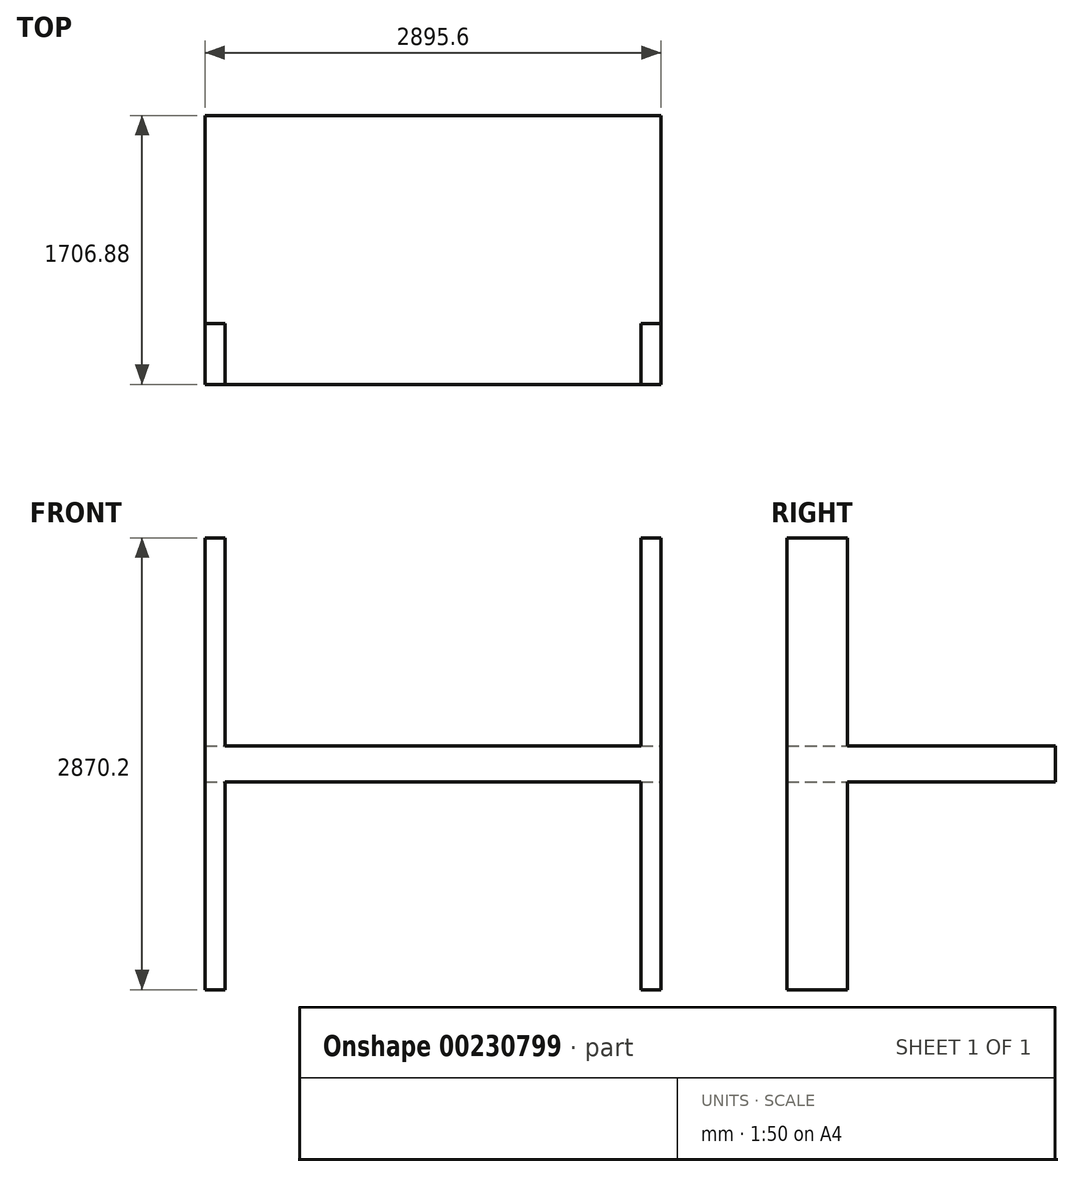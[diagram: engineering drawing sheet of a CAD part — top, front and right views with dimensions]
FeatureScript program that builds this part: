
annotation { "Feature Type Name" : "Feature", "Feature Type Description" : "" }
export const myFeature = defineFeature(function(context is Context, id is Id, definition is map)
    precondition{}
    {
        {
            var Q0;
            Q0=qCreatedBy(makeId("Front.planeOp"),FACE);
            var sketch = newSketch(context, id + "F0", { "sketchPlane" : qUnion([Q0])});
            skSolve(sketch);
        }
        {
            var Q0;
            Q0=qCreatedBy(makeId("Front.planeOp"),FACE);
            var sketch = newSketch(context, id + "F1", { "sketchPlane" : qUnion([Q0])});
            skLineSegment(sketch, "E0.bottom", {"start": v(-670.18, 381.56) * mm, "end": v(2225.42, 381.56) * mm});
            skLineSegment(sketch, "E0.top", {"start": v(-670.18, 152.96) * mm, "end": v(2225.42, 152.96) * mm});
            skLineSegment(sketch, "E0.left", {"start": v(-670.18, 381.56) * mm, "end": v(-670.18, 152.96) * mm});
            skLineSegment(sketch, "E0.right", {"start": v(2225.42, 381.56) * mm, "end": v(2225.42, 152.96) * mm});
            skLineSegment(sketch, "E1.bottom", {"start": v(-670.18, 381.56) * mm, "end": v(-543.18, 381.56) * mm});
            skLineSegment(sketch, "E1.top", {"start": v(-670.18, 1702.36) * mm, "end": v(-543.18, 1702.36) * mm});
            skLineSegment(sketch, "E1.left", {"start": v(-670.18, 381.56) * mm, "end": v(-670.18, 1702.36) * mm});
            skLineSegment(sketch, "E1.right", {"start": v(-543.18, 381.56) * mm, "end": v(-543.18, 1702.36) * mm});
            skLineSegment(sketch, "E2.bottom", {"start": v(2225.42, 381.56) * mm, "end": v(2098.42, 381.56) * mm});
            skLineSegment(sketch, "E2.top", {"start": v(2225.42, 1702.36) * mm, "end": v(2098.42, 1702.36) * mm});
            skLineSegment(sketch, "E2.left", {"start": v(2225.42, 381.56) * mm, "end": v(2225.42, 1702.36) * mm});
            skLineSegment(sketch, "E2.right", {"start": v(2098.42, 381.56) * mm, "end": v(2098.42, 1702.36) * mm});
            skLineSegment(sketch, "E3.bottom", {"start": v(-670.18, 152.96) * mm, "end": v(-543.18, 152.96) * mm});
            skLineSegment(sketch, "E3.top", {"start": v(-670.18, -1167.84) * mm, "end": v(-543.18, -1167.84) * mm});
            skLineSegment(sketch, "E3.left", {"start": v(-670.18, 152.96) * mm, "end": v(-670.18, -1167.84) * mm});
            skLineSegment(sketch, "E3.right", {"start": v(-543.18, 152.96) * mm, "end": v(-543.18, -1167.84) * mm});
            skLineSegment(sketch, "E4.bottom", {"start": v(2225.42, 152.96) * mm, "end": v(2098.42, 152.96) * mm});
            skLineSegment(sketch, "E4.top", {"start": v(2225.42, -1167.84) * mm, "end": v(2098.42, -1167.84) * mm});
            skLineSegment(sketch, "E4.left", {"start": v(2225.42, 152.96) * mm, "end": v(2225.42, -1167.84) * mm});
            skLineSegment(sketch, "E4.right", {"start": v(2098.42, 152.96) * mm, "end": v(2098.42, -1167.84) * mm});
            skSolve(sketch);
        }
        {
            var Q0;
            Q0=makeQuery(id+"F1.imprint","IMPRINT",FACE,{"disambiguationData":[TD([[makeQuery(id+"F1.imprint","IMPRINT",EDGE,{"derivedFrom":sQuery(id+"F1.wireOp",EDGE,"E0.bottom")}),-1.0]])]});
            extrude(context, id + "F2", {"entities" : qUnion([Q0]), "oppositeDirection" : true, "depth" : 1320.8 * mm});
        }
        {
            var Q0;
            Q0 = qSketchRegion(id + "F0", true);
            var Q1;
            Q1 = qSketchRegion(id + "F1", true);
            var Q2;
            Q2 = qSketchRegion(id + "FLGmvQbmq5YZHEE_1", true);
            extrude(context, id + "F3", {"entities" : qUnion([Q0, Q1, Q2]), "operationType" : NewBodyOperationType.ADD, "depth" : 386.08 * mm});
        }
    });
